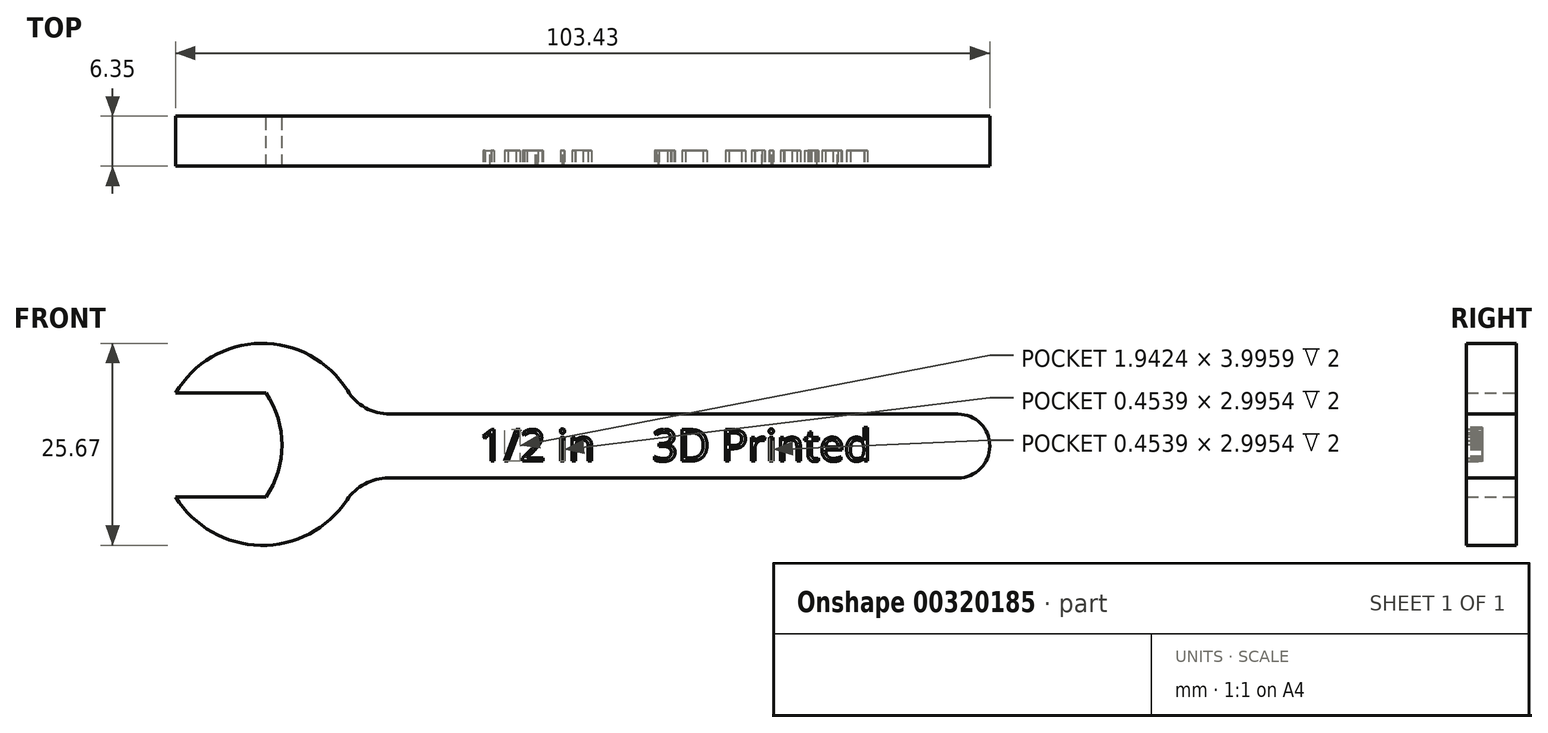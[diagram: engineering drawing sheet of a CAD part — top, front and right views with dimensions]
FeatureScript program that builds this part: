
annotation { "Feature Type Name" : "Feature", "Feature Type Description" : "" }
export const myFeature = defineFeature(function(context is Context, id is Id, definition is map)
    precondition{}
    {
        {
            var Q0;
            Q0=qCreatedBy(makeId("Front.planeOp"),FACE);
            var sketch = newSketch(context, id + "F0", { "sketchPlane" : qUnion([Q0])});
            skLineSegment(sketch, "E0.bottom", {"start": v(-18.62, 8.1) * mm, "end": v(53.55, 8.1) * mm});
            skLineSegment(sketch, "E0.top", {"start": v(-18.8, 0) * mm, "end": v(53.55, 0) * mm});
            skLineSegment(sketch, "E0.left", {"start": v(-22.65, 8.1) * mm, "end": v(-22.65, 0) * mm});
            skLineSegment(sketch, "E0.right", {"start": v(53.55, 8.1) * mm, "end": v(53.55, 0) * mm});
            skArc(sketch, "E1", {"start": v(-24.01, 11.1) * mm, "mid": v(-35.01, 17.1) * mm, "end": v(-45.83, 10.77) * mm});
            skArc(sketch, "E2", {"start": v(-45.82, -2.44) * mm, "mid": v(-35.05, -8.57) * mm, "end": v(-24.07, -2.82) * mm});
            skLineSegment(sketch, "E3", {"start": v(-45.83, 10.77) * mm, "end": v(-34.33, 10.77) * mm});
            skLineSegment(sketch, "E4", {"start": v(-34.33, -2.44) * mm, "end": v(-45.82, -2.44) * mm});
            skArc(sketch, "E5", {"start": v(-34.33, -2.44) * mm, "mid": v(-32.33, 4.16) * mm, "end": v(-34.33, 10.77) * mm});
            skArc(sketch, "E6", {"start": v(53.55, 0) * mm, "mid": v(57.6, 4.05) * mm, "end": v(53.55, 8.1) * mm});
            skPoint(sketch, "E7.visualSharp", {"position": v(-22.65, 8.1) * mm});
            skArc(sketch, "E7.filletArc", {"start": v(-24.01, 11.1) * mm, "mid": v(-21.7, 8.9) * mm, "end": v(-18.62, 8.1) * mm});
            skPoint(sketch, "E8.visualSharp", {"position": v(-22.65, 0) * mm});
            skArc(sketch, "E8.filletArc", {"start": v(-18.8, 0) * mm, "mid": v(-21.79, -0.75) * mm, "end": v(-24.07, -2.82) * mm});
            skSolve(sketch);
        }
        {
            var Q0;
            Q0 = qSketchRegion(id + "F0", true);
            extrude(context, id + "F1", {"entities" : qUnion([Q0]), "depth" : 6.35 * mm});
        }
        {
            var Q0;
            Q0=makeQuery(id+"F1.opExtrude","CAP_FACE",FACE,{"disambiguationData":[OSD([sQuery(id+"F0.wireOp",EDGE,"E0.bottom"),sQuery(id+"F0.wireOp",EDGE,"E0.top"),sQuery(id+"F0.wireOp",EDGE,"E1"),sQuery(id+"F0.wireOp",EDGE,"E2"),sQuery(id+"F0.wireOp",EDGE,"E3"),sQuery(id+"F0.wireOp",EDGE,"E4"),sQuery(id+"F0.wireOp",EDGE,"E5"),sQuery(id+"F0.wireOp",EDGE,"E6"),sQuery(id+"F0.wireOp",EDGE,"E7.filletArc"),sQuery(id+"F0.wireOp",EDGE,"E8.filletArc")])],"isStart":false});
            var sketch = newSketch(context, id + "F2", { "sketchPlane" : qUnion([Q0])});
            skText(sketch, "E9", { "text": "1/2 in     3D Printed", "fontName": "OpenSans-Regular.ttf"});
            const initialGuessF2  = {"E9": [-0.0073, 0.00213, 1, 0, 0.00403]};
            skSetInitialGuess(sketch, initialGuessF2);
            skSolve(sketch);
        }
        {
            var Q0;
            Q0 = qSketchRegion(id + "F2", true);
            extrude(context, id + "F3", {"entities" : qUnion([Q0]), "operationType" : NewBodyOperationType.REMOVE, "oppositeDirection" : true, "depth" : 2 * mm});
        }
    });
